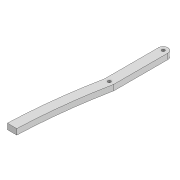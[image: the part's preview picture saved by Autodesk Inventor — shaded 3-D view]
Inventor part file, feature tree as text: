
AUTODESK INVENTOR PART (.ipt)
format: ipt  version: 2022 (Build 260153000, 153)  size: 109,056 bytes
history: native  units: mm
features: extrude x2, sketch x2
ambient origin geometry x8: Origin, YZ Plane, XZ Plane, XY Plane, X Axis, Y Axis, Z Axis, Center Point
bodies: Solid1 (feature_tree)
feature tree (4):
  extrude  "Extrusion1"  Depth=3.3mm
  extrude  "Extrusion2"  Depth=288.984mm
  sketch  "Sketch1"  dims[d0=3.3mm d1=3.3mm]
  sketch  "Sketch2"  dims[d2=10.0mm d3=288.984mm d6=6.0mm d7=0.0mm d14=3.3mm d15=231.585mm d18=600.0mm d19=600.0mm d20=10.0mm d21=0.0mm]
